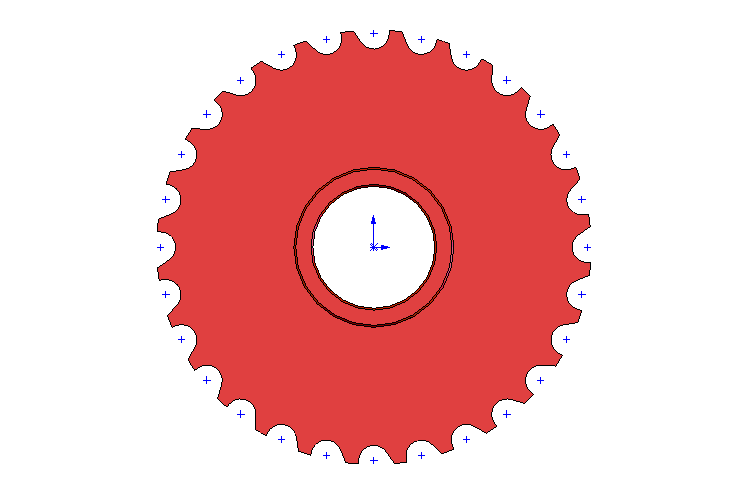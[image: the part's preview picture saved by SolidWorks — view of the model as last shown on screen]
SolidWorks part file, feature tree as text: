
SOLIDWORKS PART (.sldprt)
format: sldprt  version: not decoded by parser v0  size: 383,488 bytes
history: native  units: mm
features: sketch x4, plane x3, extrude x3, material x1, cut_extrude x1, pattern_circular x1, chamfer x1 (+10 scaffold rows collapsed)
feature tree (24):
  scaffold x10  (default folders/planes/origin — collapsed)
  material  "Matériau <non spécifié>"
  plane  "Plan de face"
  plane  "Plan de dessus"
  plane  "Plan de droite"
  sketch  "Esquisse1"  dims[D1=114.0mm]
  extrude  "Extrusion1"  Depth=2mm
  sketch  "Esquisse2"  dims[c1.D1=8.0mm c1.D3=4.0mm c2.D1=8.0mm c2.D3=4.0mm c2.D2=9.5mm c3.D3=4.0mm c3.D2=~2.039916mm c4.D2=35.0deg c4.D3=5.0mm]
  cut_extrude  "Enlèv. mat.-Extru.1"  [1 undecoded]
  pattern_circular  "Répétition circulaire1"  Count=28 Angle=12.857143deg
  sketch  "Esquisse3"  dims[D1=42.0mm]
  extrude  "Extrusion2"  Depth=4.25mm
  sketch  "Esquisse4"  dims[D1=32.0mm]
  extrude  "Enlèv. mat.-Extru.2"  [1 undecoded]
  chamfer  "Chanfrein1"  Distance=0.5mm Angle=45deg
decode coverage: 8 of 10 modeling features carry decoded parameters
note: ~ marks probable driven/reference dimensions
note: 2 parameter values undecoded
note: suppression state not decoded; provenance and decode notes live in map.json
